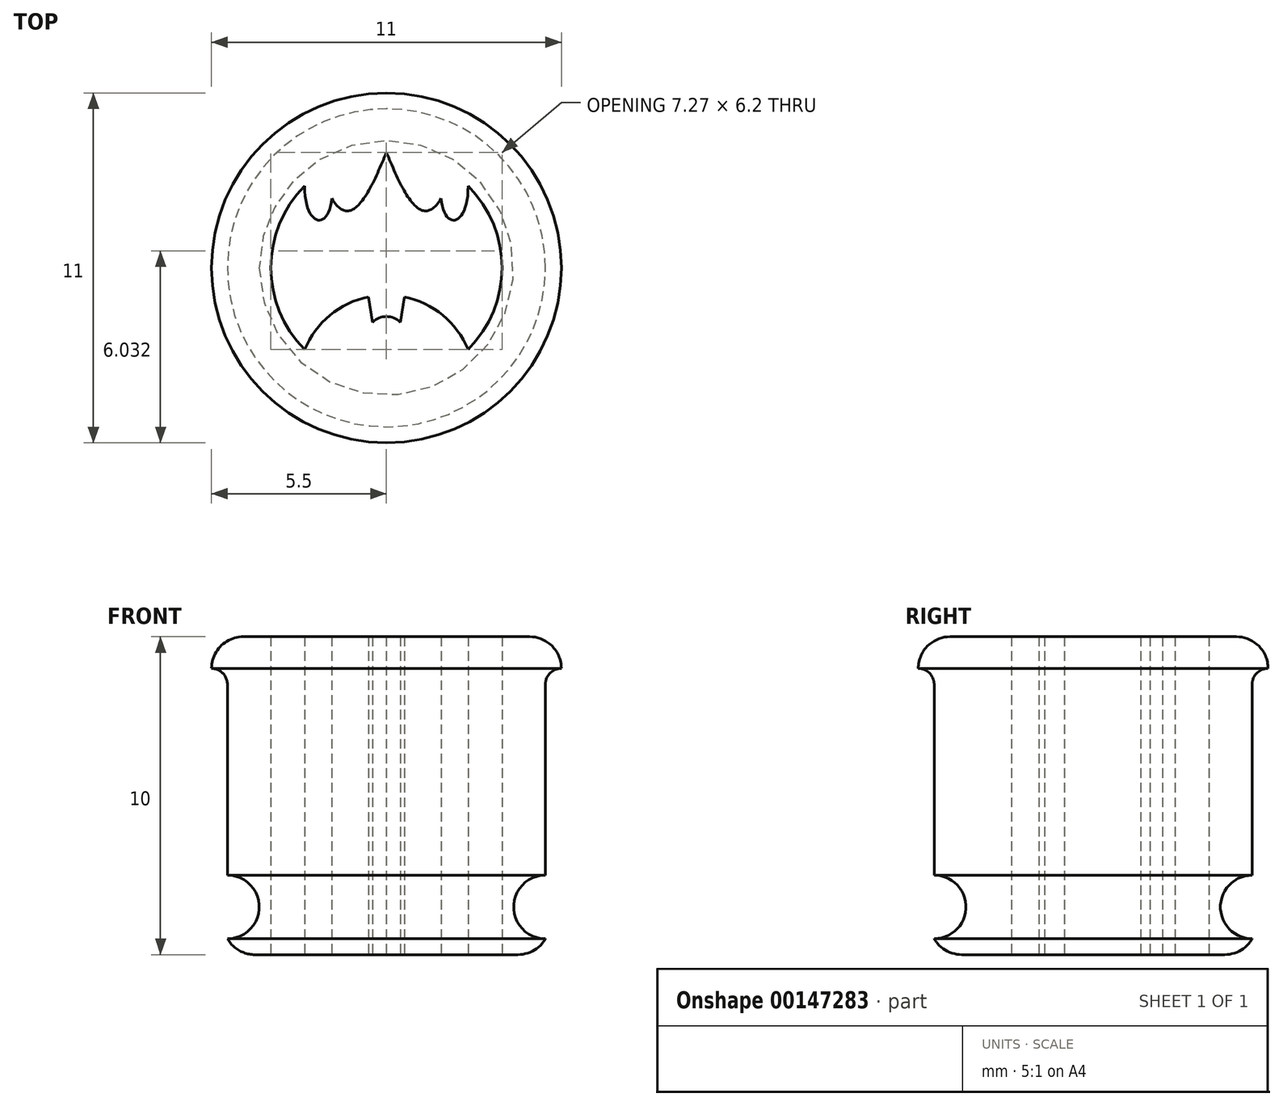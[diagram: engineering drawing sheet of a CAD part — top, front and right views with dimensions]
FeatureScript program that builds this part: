
annotation { "Feature Type Name" : "Feature", "Feature Type Description" : "" }
export const myFeature = defineFeature(function(context is Context, id is Id, definition is map)
    precondition{}
    {
        {
            var Q0;
            Q0=qCreatedBy(makeId("Front.planeOp"),FACE);
            var sketch = newSketch(context, id + "F0", { "sketchPlane" : qUnion([Q0])});
            skLineSegment(sketch, "E0.bottom", {"start": v(0, 0) * mm, "end": v(5, 0) * mm});
            skLineSegment(sketch, "E0.top", {"start": v(0, 10) * mm, "end": v(5, 10) * mm});
            skLineSegment(sketch, "E0.left", {"start": v(0, 0) * mm, "end": v(0, 10) * mm});
            skLineSegment(sketch, "E0.right", {"start": v(5, 0) * mm, "end": v(5, 8.5) * mm});
            skLineSegment(sketch, "E1.bottom", {"start": v(5, 10) * mm, "end": v(5.5, 10) * mm});
            skLineSegment(sketch, "E1.top", {"start": v(5.5, 9) * mm, "end": v(5.5, 9) * mm});
            skLineSegment(sketch, "E1.right", {"start": v(5.5, 10) * mm, "end": v(5.5, 9) * mm});
            skArc(sketch, "E2.filletArc", {"start": v(5.5, 9) * mm, "mid": v(5.15, 8.85) * mm, "end": v(5, 8.5) * mm});
            skCircle(sketch, "E3", {"center": v(5, 1.5) * mm, "radius": 1 * mm});
            skLineSegment(sketch, "E4", {"start": v(3.5, 0) * mm, "end": v(3.5, 10) * mm});
            skFitSpline(sketch, "E5", {"points": [v(5, 10) * mm, v(3.5, 0) * mm], "startDerivative": vector(-2.72, 0) * mm, "endDerivative": vector(0, -9.64) * mm});
            skSolve(sketch);
        }
        {
            var Q0;
            {var subQ7=sQuery(id+"F0.wireOp",EDGE,"E1.bottom");Q0=makeQuery(id+"F0.imprint","IMPRINT",FACE,{"disambiguationData":[TD([[makeQuery(id+"F0.imprint","IMPRINT",EDGE,{"derivedFrom":subQ7}),-1.0]])]});}
            var Q1;
            {var subQ0=sQuery(id+"F0.wireOp",EDGE,"E0.left");Q1=makeQuery(id+"F0.imprint","IMPRINT",FACE,{"disambiguationData":[TD([[makeQuery(id+"F0.imprint","IMPRINT",EDGE,{"derivedFrom":subQ0}),-1.0]])]});}
            var Q2;
            {var subQ2=sQuery(id+"F0.wireOp",EDGE,"E4");Q2=makeQuery(id+"F0.imprint","IMPRINT",FACE,{"disambiguationData":[TD([[makeQuery(id+"F0.imprint","IMPRINT",EDGE,{"derivedFrom":subQ2}),-1.0]])]});}
            var Q3;
            Q3=sQuery(id+"F0.wireOp",EDGE,"E0.left");
            revolve(context, id + "F1", {"entities" : qUnion([Q0, Q1, Q2]), "axis" : qUnion([Q3]), "revolveType" : RevolveType.FULL});
        }
        {
            var Q0;
            Q0=makeQuery(id+"F1.opRevolve","SWEPT_EDGE",EDGE,{"disambiguationData":[OSD([sQuery(id+"F0.wireOp",EDGE,"E0.top"),sQuery(id+"F0.wireOp",EDGE,"E4")])]});
            var Q1;
            Q1=makeQuery(id+"F1.opRevolve","SWEPT_EDGE",EDGE,{"disambiguationData":[OSD([sQuery(id+"F0.wireOp",EDGE,"E0.bottom"),sQuery(id+"F0.wireOp",EDGE,"E4")])]});
            var Q2;
            Q2=makeQuery(id+"F1.opRevolve","SWEPT_EDGE",EDGE,{"disambiguationData":[OSD([sQuery(id+"F0.wireOp",EDGE,"E1.bottom"),sQuery(id+"F0.wireOp",EDGE,"E1.right")])]});
            fillet(context, id + "F2", {"entities" : qUnion([Q0, Q1, Q2]), "radius" : 1 * mm, "tangentPropagation" : true, "allowEdgeOverflow" : false});
        }
        {
            var Q0;
            Q0=makeQuery(id+"F1.opRevolve","SWEPT_FACE",FACE,{"disambiguationData":[OSD([sQuery(id+"F0.wireOp",EDGE,"E0.bottom")])]});
            var sketch = newSketch(context, id + "F3", { "sketchPlane" : qUnion([Q0])});
            skCircle(sketch, "E6.0.0", {"center": v(0, 0) * mm, "radius": 4.13 * mm});
            skCircle(sketch, "E7.0", {"center": v(0, 0) * mm, "radius": 3.63 * mm});
            skLineSegment(sketch, "E8", {"start": v(0, 3.63) * mm, "end": v(0, -3.63) * mm, "construction": true});
            skLineSegment(sketch, "E9.bottom", {"start": v(-2.57, 2.57) * mm, "end": v(2.57, 2.57) * mm, "construction": true});
            skLineSegment(sketch, "E9.top", {"start": v(-2.57, -2.57) * mm, "end": v(2.57, -2.57) * mm, "construction": true});
            skLineSegment(sketch, "E9.left", {"start": v(-2.57, 2.57) * mm, "end": v(-2.57, -2.57) * mm, "construction": true});
            skLineSegment(sketch, "E9.right", {"start": v(2.57, 2.57) * mm, "end": v(2.57, -2.57) * mm, "construction": true});
            skArc(sketch, "E10", {"start": v(-2.57, 2.57) * mm, "mid": v(-1.55, 1.32) * mm, "end": v(0, 0.85) * mm});
            skLineSegment(sketch, "E11", {"start": v(-2.57, 2.57) * mm, "end": v(0, -3.63) * mm, "construction": true});
            skFitSpline(sketch, "E12", {"points": [v(-2.57, -2.57) * mm, v(-1.72, -2.18) * mm], "startDerivative": vector(0, 3.85) * mm, "endDerivative": vector(0.31, -3.09) * mm});
            skFitSpline(sketch, "E13", {"points": [v(-1.72, -2.18) * mm, v(0, -3.63) * mm], "startDerivative": vector(1.96, 3.35) * mm, "endDerivative": vector(1.32, -3.2) * mm});
            skArc(sketch, "E14", {"start": v(-0.44, 1.71) * mm, "mid": v(0, 1.53) * mm, "end": v(0.44, 1.71) * mm});
            skPoint(sketch, "E15", {"position": v(0, 1.71) * mm});
            skFitSpline(sketch, "E16.MirrorCS", {"points": [v(1.72, -2.18) * mm, v(0, -3.63) * mm], "startDerivative": vector(-1.96, 3.35) * mm, "endDerivative": vector(-1.32, -3.2) * mm});
            skFitSpline(sketch, "E17.MirrorCS", {"points": [v(2.57, -2.57) * mm, v(1.72, -2.18) * mm], "startDerivative": vector(0, 3.85) * mm, "endDerivative": vector(-0.31, -3.09) * mm});
            skArc(sketch, "E18.trimOffspring", {"start": v(0, 0.85) * mm, "mid": v(1.55, 1.32) * mm, "end": v(2.57, 2.57) * mm});
            skArc(sketch, "E19", {"start": v(2.57, -2.57) * mm, "mid": v(0, -1.9) * mm, "end": v(-2.57, -2.57) * mm});
            skCircle(sketch, "E20", {"center": v(0, -3.63) * mm, "radius": 3.48 * mm, "construction": true});
            skCircle(sketch, "E21", {"center": v(0, -1.9) * mm, "radius": 1.74 * mm, "construction": true});
            skArc(sketch, "E22", {"start": v(2.57, -1.29) * mm, "mid": v(0, -1.02) * mm, "end": v(-2.57, -1.29) * mm});
            skCircle(sketch, "E23", {"center": v(0, -1.02) * mm, "radius": 0.87 * mm, "construction": true});
            skCircle(sketch, "E24", {"center": v(-1.82, -1.15) * mm, "radius": 0.76 * mm, "construction": true});
            skArc(sketch, "E25", {"start": v(0.44, 1.71) * mm, "mid": v(0, 2.15) * mm, "end": v(-0.44, 1.71) * mm, "construction": true});
            skCircle(sketch, "E26", {"center": v(0, 1.71) * mm, "radius": 0.86 * mm, "construction": true});
            skLineSegment(sketch, "E27", {"start": v(-0.44, 1.71) * mm, "end": v(0.44, 1.71) * mm, "construction": true});
            skLineSegment(sketch, "E28", {"start": v(0.86, -0.88) * mm, "end": v(0.44, 1.71) * mm, "construction": true});
            skLineSegment(sketch, "E29", {"start": v(-0.44, 1.71) * mm, "end": v(-0.86, -0.88) * mm, "construction": true});
            skLineSegment(sketch, "E30", {"start": v(-0.44, 1.71) * mm, "end": v(-0.57, 0.91) * mm});
            skLineSegment(sketch, "E31", {"start": v(0.44, 1.71) * mm, "end": v(0.57, 0.91) * mm});
            skCircle(sketch, "E32", {"center": v(0, -0.59) * mm, "radius": 0.44 * mm, "construction": true});
            skLineSegment(sketch, "E33", {"start": v(-0.44, 1.71) * mm, "end": v(-0.44, -0.59) * mm, "construction": true});
            skSolve(sketch);
        }
        {
            var Q0;
            {var subQ4=sQuery(id+"F3.wireOp",EDGE,"E10");Q0=makeQuery(id+"F3.imprint","IMPRINT",FACE,{"disambiguationData":[TD([[makeQuery(id+"F3.imprint","IMPRINT",EDGE,{"derivedFrom":subQ4}),-1.0]])]});}
            var Q1;
            {var subQ1=sQuery(id+"F3.wireOp",EDGE,"E13");var subQ3=sQuery(id+"F3.wireOp",EDGE,"E19");var subQ4=makeQuery(id+"F3.imprint","INTERSECT",VERTEX,{"derivedFrom":[subQ1,subQ3]});Q1=makeQuery(id+"F3.imprint","IMPRINT",FACE,{"disambiguationData":[TD([[makeQuery(id+"F3.imprint","IMPRINT",EDGE,{"disambiguationData":[TD([[subQ4,1.0]])],"derivedFrom":subQ3}),1.0]])]});}
            var Q2;
            Q2=makeQuery(id+"F3.imprint","IMPRINT",FACE,{"disambiguationData":[TD([[makeQuery(id+"F3.imprint","IMPRINT",EDGE,{"derivedFrom":sQuery(id+"F3.wireOp",EDGE,"E14")}),-1.0]])]});
            extrude(context, id + "F4", {"entities" : qUnion([Q0, Q1, Q2]), "operationType" : NewBodyOperationType.REMOVE, "oppositeDirection" : true, "depth" : 25 * mm});
        }
    });
